# Revit family: WST-500-5B
name_source: partatom
category: Specialty Equipment
revit_build: Autodesk Revit 2016 (Build: 20150220_1215(x64)
units: mm (PartAtom-declared; Revit-internal decimal feet)

## family parameters
Always vertical = Yes
Cut with Voids When Loaded = No
Part Type = Normal
Room Calculation Point = No
Round Connector Dimension = Use Diameter
Shared = No
Work Plane-Based = No

## types (1)
- WST 500-5B
    A Radio_deposito = 425 mm  [stored 1.39436 ft]
    Agua caliente útil Tª salida 40ºC = 714 l
    Agua caliente útil Tª salida 45 ºC = 833 l
    Autor = 6d ingenieros
    Caudal agua intercambiador = 5900 l/h
    Caudal máximo entrada agua fría = 50 l/min
    Clase de eficiencia energética de caldeo = B
    Conexión agua caliente = R1 1/4"
    Conexión agua fría = R1 1/4"
    Conexión recirculación = R3/4"
    Contenido = 500 l
    D Altura tanque = 1868 mm  [stored 6.12861 ft]
    Description = Interacumulador de agua caliente sanitaria de 500 litros de capacidad, modelo WST 500-5B
    E = 131 mm
    F = 292 mm
    G = 928 mm
    H = 1128 mm
    I = 1731 mm  [stored 5.67913 ft]
    J = 2300 mm
    Manufacturer = BOSCH
    Model = WST 500-5B
    Peso en vacío = 179 kg
    PlasticArea = Bosch_160-160-160
    Potencia continua (80ºC imp./45ºC salida ACS/10ºC Suministro) = 66,4 kW
    Potencia máxima de calentamiento = 66,4 kW
    Presión de prueba máxima del agua caliente = 10 bar
    Presión de servicio máxima del agua potable = 10 bar
    Presión máxima intercambiador = 16 bar
    Presión nominal máxima = 7,8 bar
    Pérdida presión intercambiador (agua) = 350 mbar
    Radio Impulsión acumulador = 16 mm  [stored 0.0524934 ft]
    Radio circulación = 10 mm  [stored 0.0328084 ft]
    Radio entrada agua fría = 16 mm  [stored 0.0524934 ft]
    Radio puerta = 435 mm
    Radio retorno acumulador = 16 mm  [stored 0.0524934 ft]
    Radio salida agua caliente = 16 mm  [stored 0.0524934 ft]
    Radio sonda = 10 mm  [stored 0.0328084 ft]
    Temperatura máxima intercambiador = 160 ºC
    Tiempo calentamiento con petencia nominal = 44 min
    Tª máxima agua caliente = 95 ºC
    URL = www.bosch-thermotechnology.com/es/es/comercial-e-industrial/ocs/stora-w-st--5-742030-p
    Versión = 1.0

note: [stored X ft] marks values corroborated as IEEE doubles in the binary element streams (Revit-internal decimal feet)

## geometry (parser evidence)
native form markers: Sweep x2
no freeform markers — native parametric forms only
